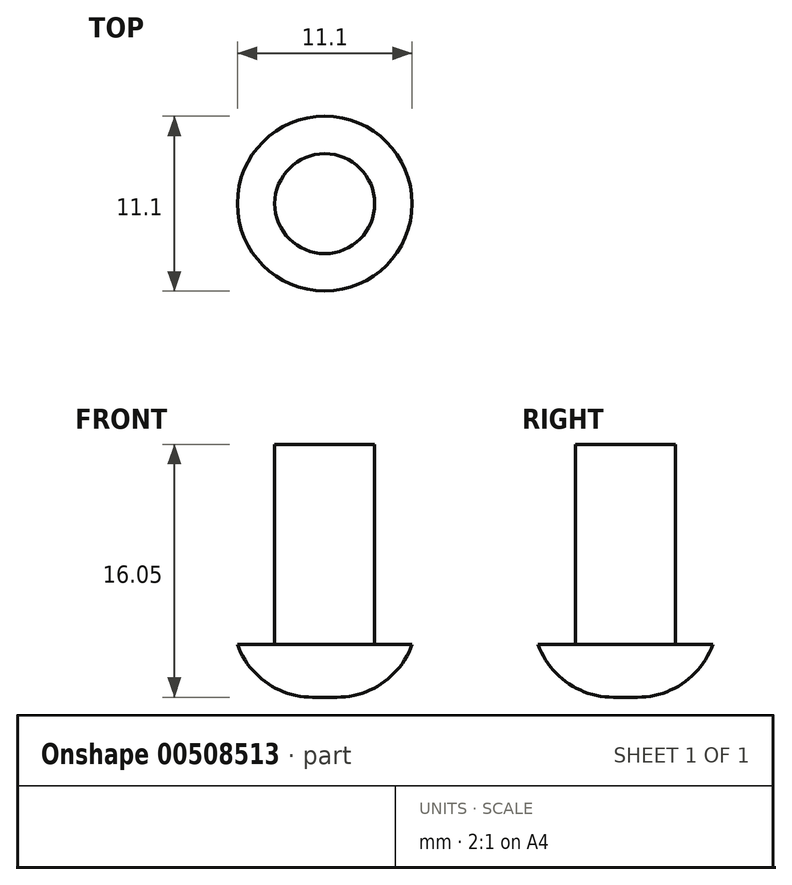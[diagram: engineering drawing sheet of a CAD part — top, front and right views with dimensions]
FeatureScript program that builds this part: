
annotation { "Feature Type Name" : "Feature", "Feature Type Description" : "" }
export const myFeature = defineFeature(function(context is Context, id is Id, definition is map)
    precondition{}
    {
        {
            var Q0;
            Q0=qCreatedBy(makeId("Top.planeOp"),FACE);
            var sketch = newSketch(context, id + "F0", { "sketchPlane" : qUnion([Q0])});
            skCircle(sketch, "E0", {"center": v(0, 0) * mm, "radius": 5.55 * mm});
            skSolve(sketch);
        }
        {
            var Q0;
            Q0=makeQuery(id+"F0.imprint","IMPRINT",FACE,{"disambiguationData":[TD([[makeQuery(id+"F0.imprint","IMPRINT",EDGE,{"derivedFrom":sQuery(id+"F0.wireOp",EDGE,"E0")}),1.0]])]});
            extrude(context, id + "F1", {"entities" : qUnion([Q0]), "depth" : 3.35 * mm, "offsetDistance" : 25.4 * mm});
        }
        {
            var Q0;
            Q0=makeQuery(id+"F1.opExtrude","CAP_FACE",FACE,{"disambiguationData":[OSD([sQuery(id+"F0.wireOp",EDGE,"E0")])],"isStart":false});
            var sketch = newSketch(context, id + "F2", { "sketchPlane" : qUnion([Q0])});
            skCircle(sketch, "E1", {"center": v(0, 0) * mm, "radius": 3.18 * mm});
            skSolve(sketch);
        }
        {
            var Q0;
            Q0=makeQuery(id+"F2.imprint","IMPRINT",FACE,{"disambiguationData":[TD([[makeQuery(id+"F2.imprint","IMPRINT",EDGE,{"derivedFrom":sQuery(id+"F2.wireOp",EDGE,"E1")}),1.0]])]});
            extrude(context, id + "F3", {"entities" : qUnion([Q0]), "operationType" : NewBodyOperationType.ADD, "depth" : 12.7 * mm, "offsetDistance" : 25.4 * mm});
        }
        {
            var Q0;
            Q0=makeQuery(id+"F1.opExtrude","CAP_EDGE",EDGE,{"disambiguationData":[OSD([sQuery(id+"F0.wireOp",EDGE,"E0")])],"isStart":true});
            fillet(context, id + "F4", {"entities" : qUnion([Q0]), "radius" : 5.08 * mm, "tangentPropagation" : true, "allowEdgeOverflow" : false});
        }
    });
